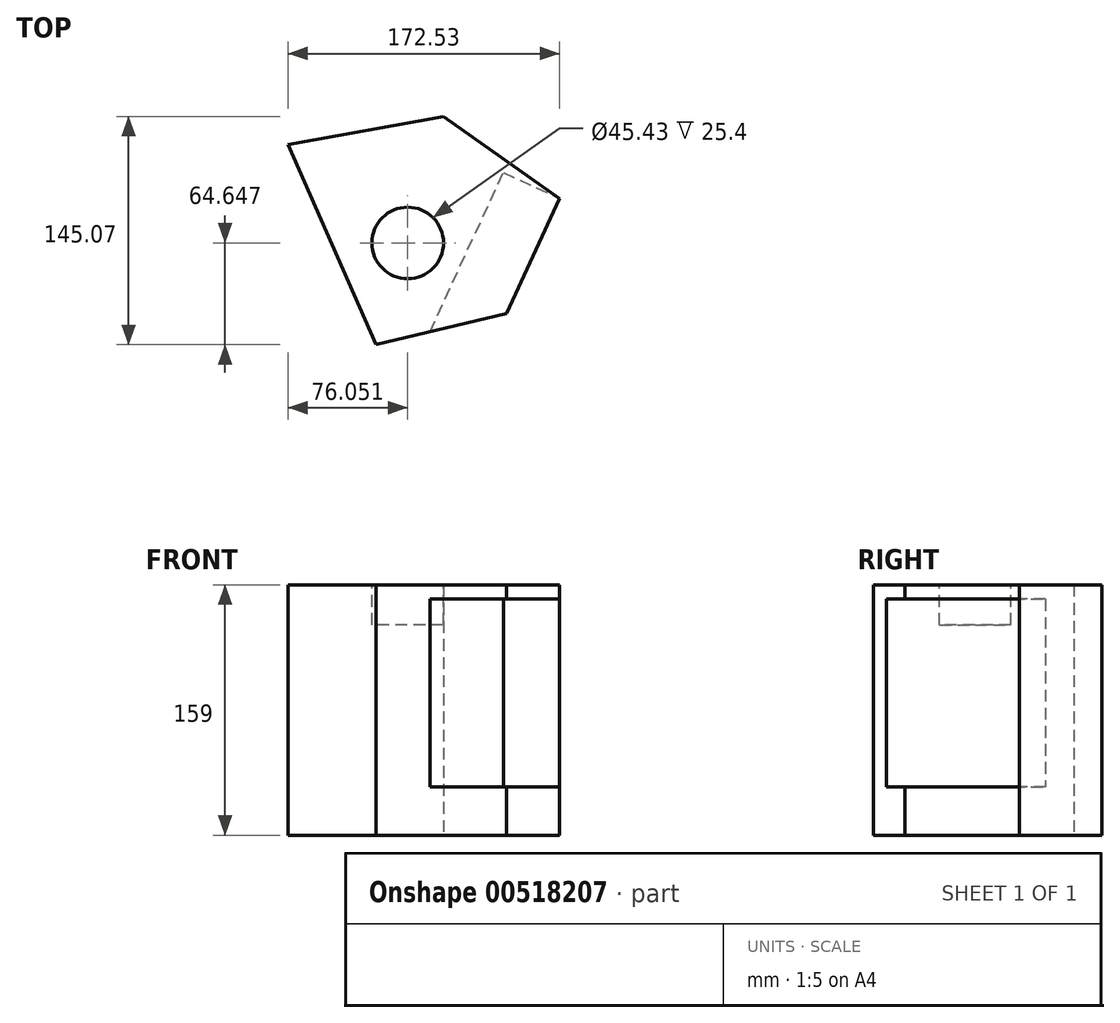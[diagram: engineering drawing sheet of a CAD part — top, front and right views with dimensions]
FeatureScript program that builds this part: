
annotation { "Feature Type Name" : "Feature", "Feature Type Description" : "" }
export const myFeature = defineFeature(function(context is Context, id is Id, definition is map)
    precondition{}
    {
        {
            var Q0;
            Q0=qCreatedBy(makeId("Top.planeOp"),FACE);
            var sketch = newSketch(context, id + "F0", { "sketchPlane" : qUnion([Q0])});
            skLineSegment(sketch, "E0", {"start": v(-70.35, -81.42) * mm, "end": v(-126.45, 45.77) * mm});
            skLineSegment(sketch, "E1", {"start": v(-126.45, 45.77) * mm, "end": v(-27.57, 63.65) * mm});
            skLineSegment(sketch, "E2", {"start": v(-27.57, 63.65) * mm, "end": v(46.08, 11.47) * mm});
            skLineSegment(sketch, "E3", {"start": v(46.08, 11.47) * mm, "end": v(12.42, -61.56) * mm});
            skLineSegment(sketch, "E4", {"start": v(12.42, -61.56) * mm, "end": v(-70.35, -81.42) * mm});
            skSolve(sketch);
        }
        {
            var Q0;
            Q0 = qSketchRegion(id + "F0", true);
            extrude(context, id + "F1", {"entities" : qUnion([Q0]), "depth" : 159 * mm, "offsetDistance" : 25.4 * mm});
        }
        {
            var Q0;
            Q0=makeQuery(id+"F1.opExtrude","CAP_FACE",FACE,{"disambiguationData":[OSD([sQuery(id+"F0.wireOp",EDGE,"E0"),sQuery(id+"F0.wireOp",EDGE,"E1"),sQuery(id+"F0.wireOp",EDGE,"E2"),sQuery(id+"F0.wireOp",EDGE,"E3"),sQuery(id+"F0.wireOp",EDGE,"E4")])],"isStart":false});
            var sketch = newSketch(context, id + "F2", { "sketchPlane" : qUnion([Q0])});
            skCircle(sketch, "E5", {"center": v(-50.4, -16.77) * mm, "radius": 22.72 * mm});
            skSolve(sketch);
        }
        {
            var Q0;
            Q0 = qSketchRegion(id + "F2", true);
            extrude(context, id + "F3", {"entities" : qUnion([Q0]), "operationType" : NewBodyOperationType.REMOVE, "oppositeDirection" : true, "depth" : 25.4 * mm, "offsetDistance" : 25.4 * mm});
        }
        {
            var Q0;
            Q0=makeQuery(id+"F1.opExtrude","SWEPT_FACE",FACE,{"disambiguationData":[OSD([sQuery(id+"F0.wireOp",EDGE,"E3")])]});
            var sketch = newSketch(context, id + "F4", { "sketchPlane" : qUnion([Q0])});
            skLineSegment(sketch, "E6.bottom", {"start": v(-82.33, 149.9) * mm, "end": v(29.71, 149.9) * mm});
            skLineSegment(sketch, "E6.top", {"start": v(-82.33, 30.67) * mm, "end": v(29.71, 30.67) * mm});
            skLineSegment(sketch, "E6.left", {"start": v(-82.33, 149.9) * mm, "end": v(-82.33, 30.67) * mm});
            skLineSegment(sketch, "E6.right", {"start": v(29.71, 149.9) * mm, "end": v(29.71, 30.67) * mm});
            skSolve(sketch);
        }
        {
            var Q0;
            Q0 = qSketchRegion(id + "F4", true);
            extrude(context, id + "F5", {"entities" : qUnion([Q0]), "operationType" : NewBodyOperationType.REMOVE, "oppositeDirection" : true, "depth" : 39.37 * mm, "offsetDistance" : 25.4 * mm});
        }
    });
